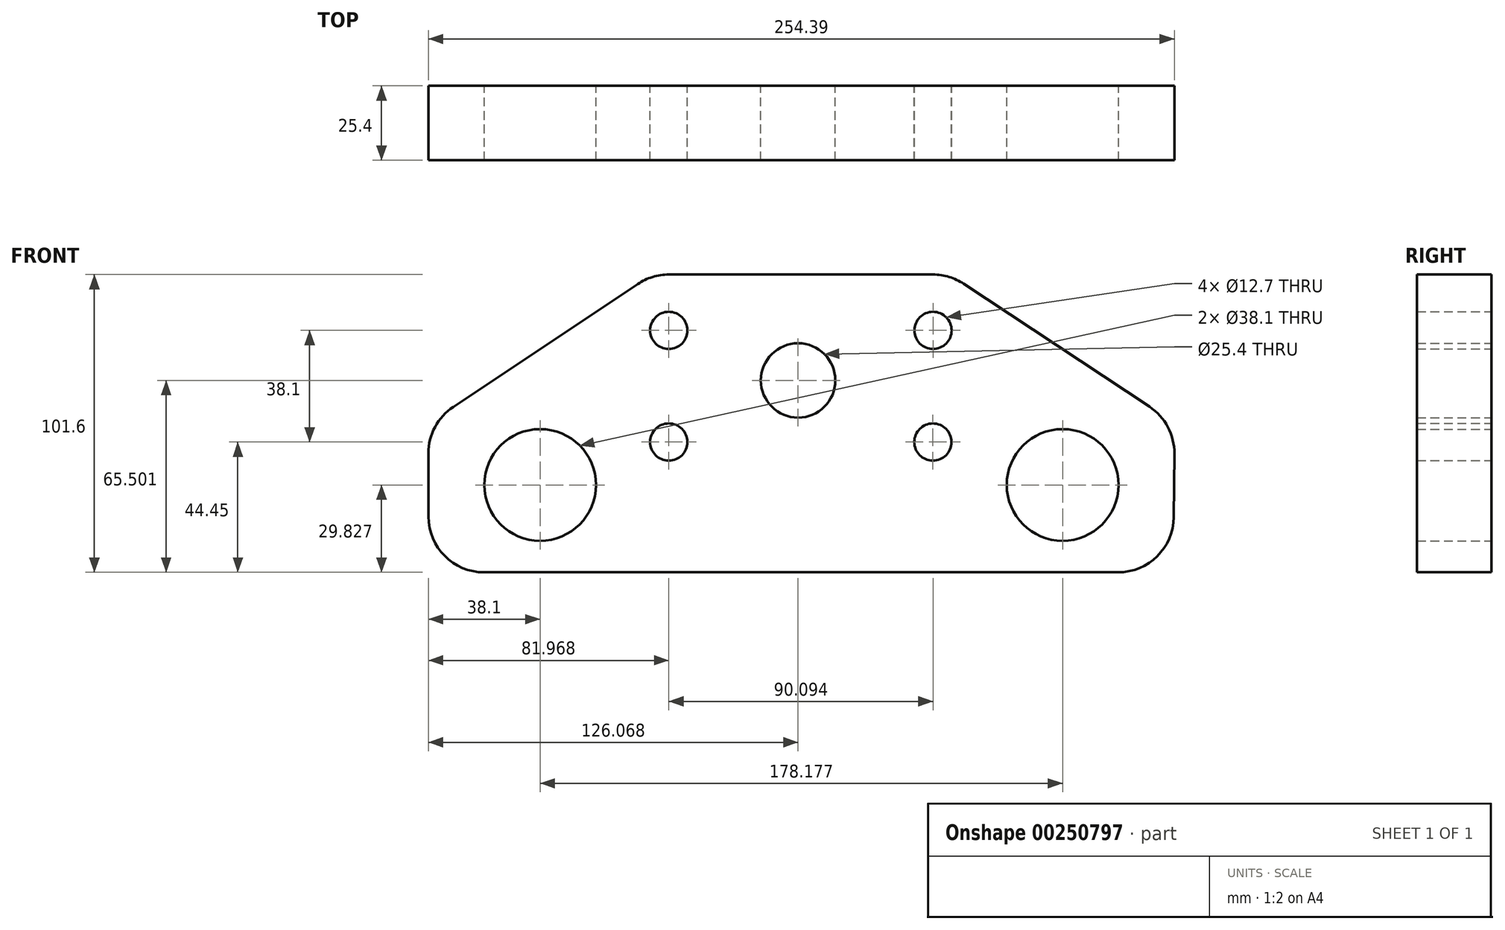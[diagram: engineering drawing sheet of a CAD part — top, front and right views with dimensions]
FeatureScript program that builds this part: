
annotation { "Feature Type Name" : "Feature", "Feature Type Description" : "" }
export const myFeature = defineFeature(function(context is Context, id is Id, definition is map)
    precondition{}
    {
        {
            var Q0;
            Q0=qCreatedBy(makeId("Front.planeOp"),FACE);
            var sketch = newSketch(context, id + "F1", { "sketchPlane" : qUnion([Q0])});
            skLineSegment(sketch, "E0", {"start": v(19.05, 0) * mm, "end": v(235.13, 0) * mm});
            skLineSegment(sketch, "E1", {"start": v(254.18, 18.87) * mm, "end": v(254.39, 40.45) * mm});
            skLineSegment(sketch, "E2", {"start": v(0, 19.05) * mm, "end": v(0, 40.6) * mm});
            skPoint(sketch, "E3", {"position": v(0, 0) * mm});
            skLineSegment(sketch, "E4", {"start": v(127, 101.6) * mm, "end": v(127, 0) * mm, "construction": true});
            skPoint(sketch, "E4.startSnap0", {"position": v(127, 0) * mm});
            skLineSegment(sketch, "E5", {"start": v(127, 101.6) * mm, "end": v(172.06, 101.6) * mm});
            skLineSegment(sketch, "E6", {"start": v(127, 101.6) * mm, "end": v(81.97, 101.6) * mm});
            skLineSegment(sketch, "E7", {"start": v(71.4, 98.4) * mm, "end": v(8.48, 56.46) * mm});
            skLineSegment(sketch, "E8", {"start": v(182.58, 98.43) * mm, "end": v(245.86, 56.51) * mm});
            skPoint(sketch, "E9.visualSharp", {"position": v(254.48, 50.8) * mm});
            skArc(sketch, "E9.filletArc", {"start": v(254.39, 40.45) * mm, "mid": v(252.16, 49.56) * mm, "end": v(245.86, 56.51) * mm});
            skPoint(sketch, "E10.visualSharp", {"position": v(254, 0) * mm});
            skArc(sketch, "E10.filletArc", {"start": v(235.13, 0) * mm, "mid": v(248.54, 5.52) * mm, "end": v(254.18, 18.87) * mm});
            skPoint(sketch, "E11.visualSharp", {"position": v(177.8, 101.6) * mm});
            skArc(sketch, "E11.filletArc", {"start": v(182.58, 98.43) * mm, "mid": v(177.56, 100.8) * mm, "end": v(172.06, 101.6) * mm});
            skPoint(sketch, "E12.visualSharp", {"position": v(76.2, 101.6) * mm});
            skArc(sketch, "E12.filletArc", {"start": v(81.97, 101.6) * mm, "mid": v(76.45, 100.78) * mm, "end": v(71.4, 98.4) * mm});
            skPoint(sketch, "E13.visualSharp", {"position": v(0, 50.8) * mm});
            skArc(sketch, "E13.filletArc", {"start": v(8.48, 56.46) * mm, "mid": v(2.25, 49.6) * mm, "end": v(0, 40.6) * mm});
            skArc(sketch, "E14.filletArc", {"start": v(0, 19.05) * mm, "mid": v(5.58, 5.58) * mm, "end": v(19.05, 0) * mm});
            skLineSegment(sketch, "E15", {"start": v(0, 29.83) * mm, "end": v(38.1, 29.83) * mm, "construction": true});
            skCircle(sketch, "E16", {"center": v(38.1, 29.83) * mm, "radius": 19.05 * mm});
            skLineSegment(sketch, "E17", {"start": v(254.39, 29.66) * mm, "end": v(216.29, 29.66) * mm, "construction": true});
            skPoint(sketch, "E17.startSnap0", {"position": v(254.28, 29.66) * mm});
            skCircle(sketch, "E18", {"center": v(216.28, 29.83) * mm, "radius": 19.05 * mm});
            skLineSegment(sketch, "E19", {"start": v(127, 101.6) * mm, "end": v(127, 63.5) * mm});
            skCircle(sketch, "E20", {"center": v(126.07, 65.5) * mm, "radius": 12.7 * mm});
            skLineSegment(sketch, "E21", {"start": v(81.97, 44.45) * mm, "end": v(81.97, 82.55) * mm});
            skLineSegment(sketch, "E22.MirrorCS", {"start": v(172.03, 44.45) * mm, "end": v(172.03, 82.55) * mm});
            skCircle(sketch, "E23", {"center": v(81.97, 82.55) * mm, "radius": 6.35 * mm});
            skCircle(sketch, "E24", {"center": v(81.97, 44.45) * mm, "radius": 6.35 * mm});
            skCircle(sketch, "E25", {"center": v(172.06, 82.55) * mm, "radius": 6.35 * mm});
            skCircle(sketch, "E26", {"center": v(172.03, 44.45) * mm, "radius": 6.35 * mm});
            skSolve(sketch);
        }
        {
            var Q0;
            Q0=makeQuery(id+"F1.imprint","IMPRINT",FACE,{"disambiguationData":[TD([[makeQuery(id+"F1.imprint","IMPRINT",EDGE,{"derivedFrom":sQuery(id+"F1.wireOp",EDGE,"E0")}),1.0]])]});
            extrude(context, id + "F2", {"entities" : qUnion([Q0]), "depth" : 25.4 * mm});
        }
    });
